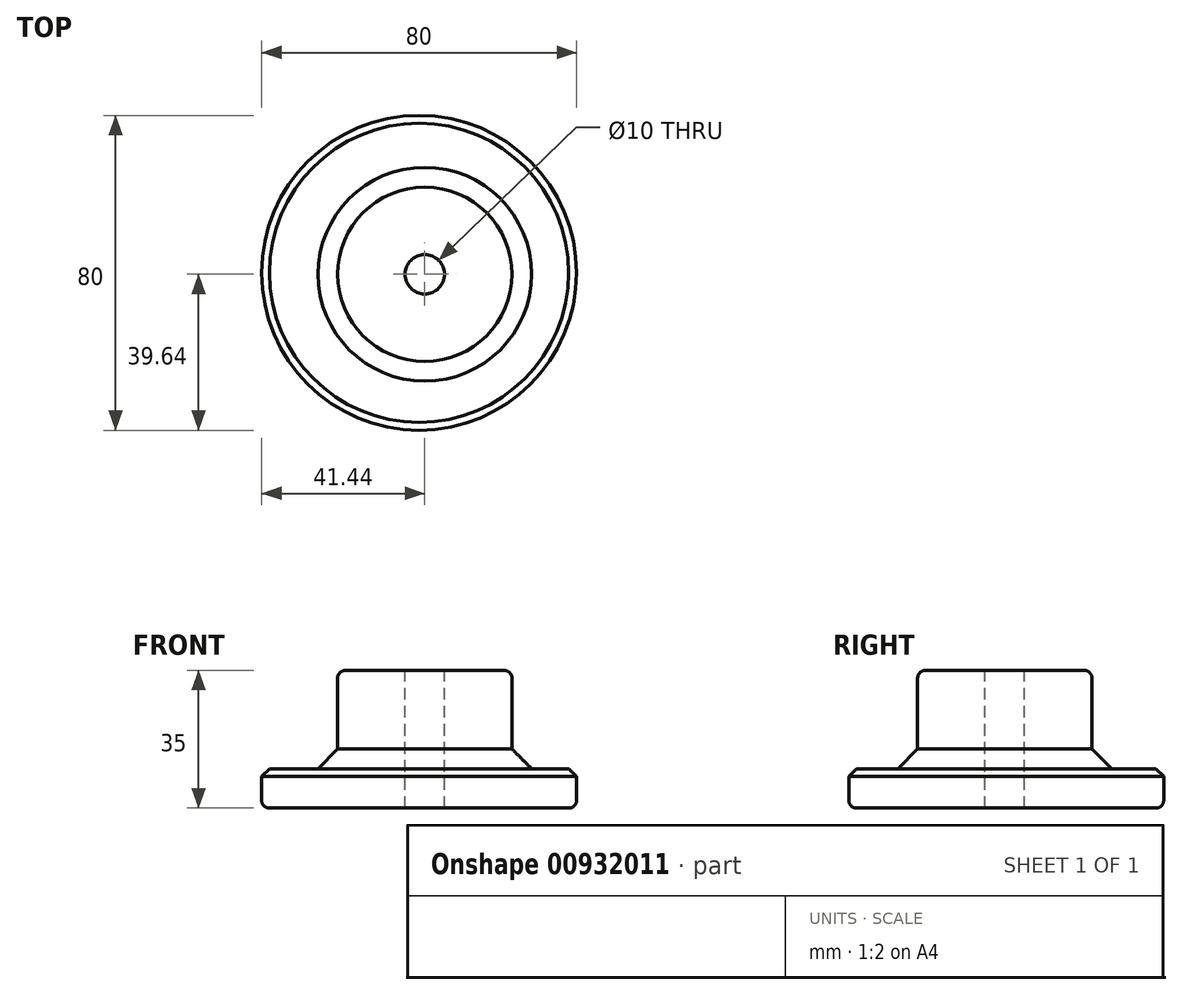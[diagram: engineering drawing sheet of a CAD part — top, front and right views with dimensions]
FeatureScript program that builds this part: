
annotation { "Feature Type Name" : "Feature", "Feature Type Description" : "" }
export const myFeature = defineFeature(function(context is Context, id is Id, definition is map)
    precondition{}
    {
        {
            var Q0;
            Q0=qCreatedBy(makeId("Top.planeOp"),FACE);
            var sketch = newSketch(context, id + "F0", { "sketchPlane" : qUnion([Q0])});
            skCircle(sketch, "E0", {"center": v(-1.44, 0.36) * mm, "radius": 40 * mm});
            skSolve(sketch);
        }
        {
            var Q0;
            Q0=makeQuery(id+"F0.imprint","IMPRINT",FACE,{"disambiguationData":[TD([[makeQuery(id+"F0.imprint","IMPRINT",EDGE,{"derivedFrom":sQuery(id+"F0.wireOp",EDGE,"E0")}),1.0]])]});
            extrude(context, id + "F1", {"entities" : qUnion([Q0]), "depth" : 10 * mm, "offsetDistance" : 25 * mm});
        }
        {
            var Q0;
            Q0=makeQuery(id+"F1.opExtrude","CAP_EDGE",EDGE,{"disambiguationData":[OSD([sQuery(id+"F0.wireOp",EDGE,"E0")])],"isStart":false});
            chamfer(context, id + "F2", {"entities" : qUnion([Q0]), "width" : 2 * mm, "tangentPropagation" : true});
        }
        {
            var Q0;
            Q0=makeQuery(id+"F1.opExtrude","CAP_FACE",FACE,{"disambiguationData":[OSD([sQuery(id+"F0.wireOp",EDGE,"E0")])],"isStart":false});
            var sketch = newSketch(context, id + "F3", { "sketchPlane" : qUnion([Q0])});
            skCircle(sketch, "E1", {"center": v(0, 0) * mm, "radius": 22.15 * mm});
            skSolve(sketch);
        }
        {
            var Q0;
            Q0=makeQuery(id+"F3.imprint","IMPRINT",FACE,{"disambiguationData":[TD([[makeQuery(id+"F3.imprint","IMPRINT",EDGE,{"derivedFrom":sQuery(id+"F3.wireOp",EDGE,"E1")}),1.0]])]});
            extrude(context, id + "F4", {"entities" : qUnion([Q0]), "operationType" : NewBodyOperationType.ADD, "depth" : 25 * mm, "offsetDistance" : 25 * mm});
        }
        {
            var Q0;
            Q0=makeQuery(id+"F4.opExtrude","CAP_FACE",FACE,{"disambiguationData":[OSD([sQuery(id+"F3.wireOp",EDGE,"E1")])],"isStart":false});
            var sketch = newSketch(context, id + "F5", { "sketchPlane" : qUnion([Q0])});
            skCircle(sketch, "E2", {"center": v(0, 0) * mm, "radius": 12.9 * mm});
            skSolve(sketch);
        }
        {
            var Q0;
            Q0=sQuery(id+"F5.wireOp",VERTEX,"E2.center");
            var Q1;
            Q1=makeQuery(id+"F1.opExtrude","SWEPT_BODY",BODY,{"disambiguationData":[OSD([sQuery(id+"F0.wireOp",EDGE,"E0")])]});
            hole(context, id + "F6", {"style" : HoleStyle.SIMPLE, "endStyle" : HoleEndStyle.THROUGH, "holeDiameter" : 10 * mm, "majorDiameter" : 5 * mm, "isTappedThrough" : true, "tappedDepth" : 12 * mm, "tapClearance" : 3, "locations" : qUnion([Q0]), "scope" : qUnion([Q1])});
        }
        {
            var Q0;
            Q0=makeQuery(id+"F1.opExtrude","CAP_EDGE",EDGE,{"disambiguationData":[OSD([sQuery(id+"F0.wireOp",EDGE,"E0")])],"isStart":true});
            var Q1;
            Q1=makeQuery(id+"F6.hole-0.boolean.opBoolean","INTERSECT",EDGE,{"derivedFrom":[makeQuery(id+"F1.opExtrude","CAP_FACE",FACE,{"disambiguationData":[OSD([sQuery(id+"F0.wireOp",EDGE,"E0")])],"isStart":true}),makeQuery(id+"F6.hole-0.opRevolve","SWEPT_FACE",FACE,{"disambiguationData":[OSD([sQuery(id+"F6.hole-0.sketch.wireOp",EDGE,"core_line_2")])]})]});
            var Q2;
            Q2=makeQuery(id+"F4.opExtrude","CAP_EDGE",EDGE,{"disambiguationData":[OSD([sQuery(id+"F3.wireOp",EDGE,"E1")])],"isStart":false});
            fillet(context, id + "F7", {"entities" : qUnion([Q0, Q1, Q2]), "radius" : 2 * mm, "tangentPropagation" : true, "allowEdgeOverflow" : false});
        }
        {
            var Q0;
            Q0=makeQuery(id+"F4.opExtrude","SWEPT_FACE",FACE,{"disambiguationData":[OSD([sQuery(id+"F3.wireOp",EDGE,"E1")])]});
            chamfer(context, id + "F8", {"entities" : qUnion([Q0]), "width" : 5 * mm, "tangentPropagation" : true});
        }
    });
